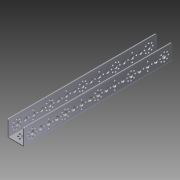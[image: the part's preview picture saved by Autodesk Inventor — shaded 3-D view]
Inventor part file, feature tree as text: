
AUTODESK INVENTOR PART (.ipt)
format: ipt  version: 2013 (Build 170138000, 138)  size: 477,696 bytes
history: native  units: in
note: dims shown in document units (in); Inventor stores cm internally (conversion verified against a paired STEP export)
features: other x1, imported_body x1, move_body x1, plane x1
ambient origin geometry x8: Origin, YZ Plane, XZ Plane, XY Plane, X Axis, Y Axis, Z Axis, Center Point
feature tree (4):
  other  "CHANNEL_288_2011"
  imported_body  "Base1"
  move_body  "Move Body1"
  plane  "Work Plane3"
